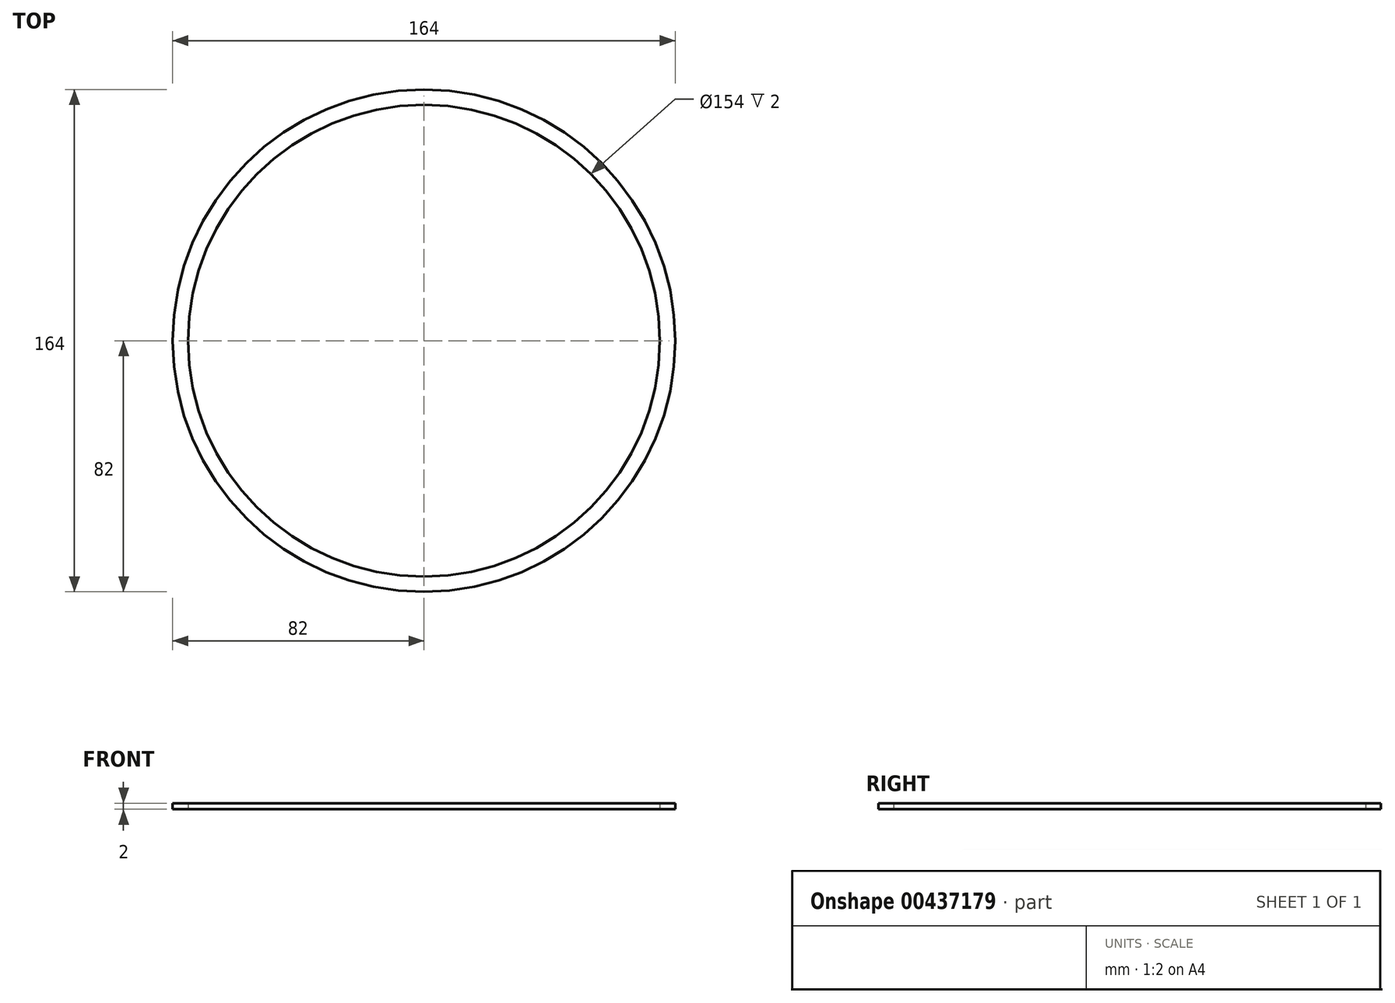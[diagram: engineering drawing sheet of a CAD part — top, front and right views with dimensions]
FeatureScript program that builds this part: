
annotation { "Feature Type Name" : "Feature", "Feature Type Description" : "" }
export const myFeature = defineFeature(function(context is Context, id is Id, definition is map)
    precondition{}
    {
        {
            var Q0;
            Q0=qCreatedBy(makeId("Top.planeOp"),FACE);
            var sketch = newSketch(context, id + "F0", { "sketchPlane" : qUnion([Q0])});
            skCircle(sketch, "E0", {"center": v(0, 0) * mm, "radius": 77 * mm});
            skCircle(sketch, "E1", {"center": v(0, 0) * mm, "radius": 82 * mm});
            skSolve(sketch);
        }
        {
            var Q0;
            Q0=makeQuery(id+"F0.imprint","IMPRINT",FACE,{"disambiguationData":[TD([[makeQuery(id+"F0.imprint","IMPRINT",EDGE,{"derivedFrom":sQuery(id+"F0.wireOp",EDGE,"E0")}),-1.0]])]});
            extrude(context, id + "F1", {"entities" : qUnion([Q0]), "depth" : 2 * mm});
        }
    });
